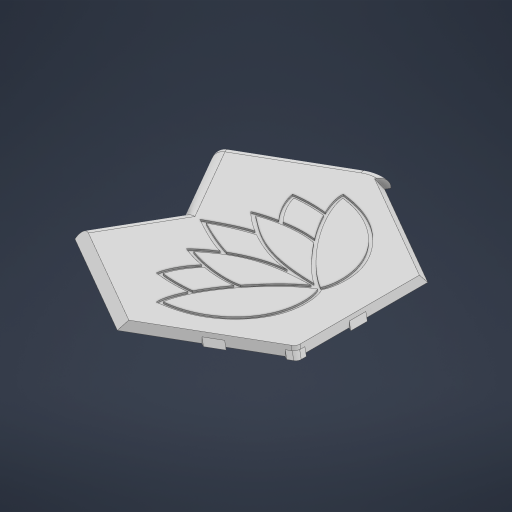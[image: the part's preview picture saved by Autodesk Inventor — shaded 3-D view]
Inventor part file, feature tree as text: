
AUTODESK INVENTOR PART (.ipt)
format: ipt  version: 2023 (Build 270158000, 158)  size: 1,570,304 bytes
history: native  units: in
note: dims shown in document units (in); Inventor stores cm internally (conversion verified against a paired STEP export)
features: extrude x9, sketch x6, direct_edit x4, fillet x4, move_body x4, draft x3
ambient origin geometry x8: Origin, YZ Plane, XZ Plane, XY Plane, X Axis, Y Axis, Z Axis, Center Point
bodies: Body1 (feature_tree)
feature tree (30):
  sketch  "Sketch2"  dims[d11=0.128in d12=0.0in d15=0.2405in]
  extrude  "Extrusion2"  Depth=0.128in
  draft  "FaceDraft1"
  extrude  "Extrusion3"  Depth=0.0394in TaperAngle=0.0deg
  extrude  "Extrusion4"  TaperAngle=120.0deg  [1 undecoded]
  sketch  "Sketch3"  dims[d20=0.128in d21=0.0in d35=0.0394in d36=0.0in]
  extrude  "Extrusion5"  TaperAngle=60.0deg  [1 undecoded]
  draft  "FaceDraft2"
  draft  "FaceDraft3"
  direct_edit  "Direct Edit1"
  direct_edit  "Direct Edit2"
  extrude  "Extrusion6"  Depth=0.0886in
  fillet  "Fillet1"  Radius=0.0886in
  fillet  "Fillet2"  Radius=0.1772in
  extrude  "Extrusion7"  Depth=0.2756in TaperAngle=0.0deg
  extrude  "Extrusion8"  [1 undecoded]
  fillet  "Fillet3"  Radius=0.3779in
  fillet  "Fillet4"  Radius=0.0787in
  direct_edit  "Direct Edit3"
  direct_edit  "Direct Edit4"
  extrude  "Extrusion9"  Depth=0.2756in TaperAngle=0.0deg
  extrude  "Extrusion10"  Depth=0.2756in TaperAngle=0.0deg
  sketch  "Sketch4"  dims[d46=0.6496in d47=120.0deg]
  sketch  "Sketch5"  dims[d48=0.6496in d49=60.0deg]
  sketch  "Sketch6"  dims[d50=0.0787in d53=0.0886in d54=0.0886in d58=0.1772in]
  sketch  "Sketch7"  dims[d59=30.0deg d60=0.0709in d61=0.0in d62=-0.3779in d63=0.3779in d64=0.0787in d65=0.0in d66=0.0in d67=0.561in d68=0.0in d69=0.0in d70=0.561in d71=0.0886in d72=0.0in d73=0.0787in d74=0.0787in d98=0.0787in d99=0.0787in d100=0.0787in d101=0.0787in d102=0.0787in d103=0.0787in d104=0.0787in d105=0.1772in d106=0.1772in d107=0.1772in d108=60.0deg d109=60.0deg d110=0.1673in d111=0.1299in d113=0.0787in d114=2.6181in d115=1.5748in d116=120.0deg d117=0.0787in d254=0.0197in d255=0.0in d256=0.7874in d257=0.3937in d258=0.0in d259=0.1181in d260=0.1181in d261=0.0in d262=0.0in d263=-0.0118in d264=120.0deg d265=0.892in d266=1.478in d267=0.0in d268=0.0in d269=-0.0157in d270=0.0846in d271=0.1496in d273=0.1378in d274=0.1378in d275=0.0827in d276=0.0in d277=0.1969in d278=0.2756in d279=0.0in d37=0.0197in d38=0.0344in d75=0.0197in d76=0.0344in d77=0.0197in d78=0.0344in]
  move_body  "Move1"
  move_body  "Move2"
  move_body  "Move3"
  move_body  "Move4"
note: 3 required parameter values undecoded (feature->parameter linkage not recoverable at this tier; creation-order binding heuristic only, values carry confidence <= 0.55)
